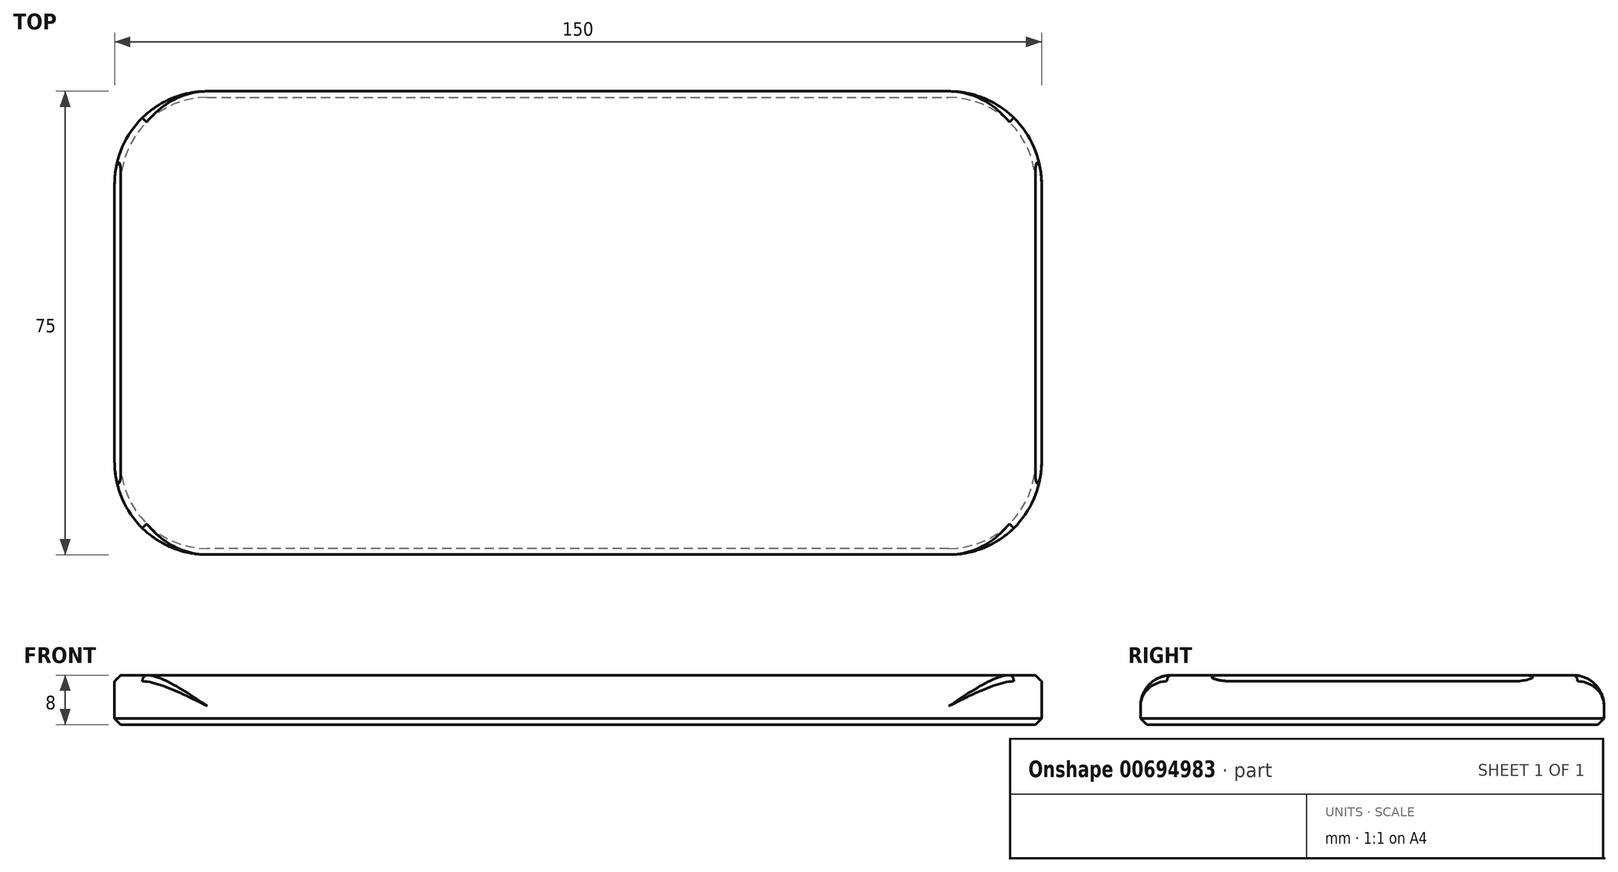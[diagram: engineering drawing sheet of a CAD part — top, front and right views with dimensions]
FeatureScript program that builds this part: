
annotation { "Feature Type Name" : "Feature", "Feature Type Description" : "" }
export const myFeature = defineFeature(function(context is Context, id is Id, definition is map)
    precondition{}
    {
        {
            var Q0;
            Q0=qCreatedBy(makeId("Top.planeOp"),FACE);
            var sketch = newSketch(context, id + "F0", { "sketchPlane" : qUnion([Q0])});
            skLineSegment(sketch, "E0.bottom", {"start": v(73.47, 26.68) * mm, "end": v(-76.53, 26.68) * mm});
            skLineSegment(sketch, "E0.top", {"start": v(73.47, -48.32) * mm, "end": v(-76.53, -48.32) * mm});
            skLineSegment(sketch, "E0.left", {"start": v(73.47, 26.68) * mm, "end": v(73.47, -48.32) * mm});
            skLineSegment(sketch, "E0.right", {"start": v(-76.53, 26.68) * mm, "end": v(-76.53, -48.32) * mm});
            skSolve(sketch);
        }
        {
            var Q0;
            Q0=makeQuery(id+"F0.imprint","IMPRINT",FACE,{"disambiguationData":[TD([[makeQuery(id+"F0.imprint","IMPRINT",EDGE,{"derivedFrom":sQuery(id+"F0.wireOp",EDGE,"E0.bottom")}),1.0]])]});
            extrude(context, id + "F1", {"entities" : qUnion([Q0]), "depth" : 8 * mm, "offsetDistance" : 25 * mm});
        }
        {
            var Q0;
            Q0=makeQuery(id+"F1.opExtrude","CAP_EDGE",EDGE,{"disambiguationData":[OSD([sQuery(id+"F0.wireOp",EDGE,"E0.left")])],"isStart":false});
            var Q1;
            Q1=makeQuery(id+"F1.opExtrude","CAP_EDGE",EDGE,{"disambiguationData":[OSD([sQuery(id+"F0.wireOp",EDGE,"E0.right")])],"isStart":false});
            chamfer(context, id + "F2", {"entities" : qUnion([Q0, Q1]), "width" : 1 * mm, "tangentPropagation" : true});
        }
        {
            var Q0;
            Q0=makeQuery(id+"F1.opExtrude","CAP_EDGE",EDGE,{"disambiguationData":[OSD([sQuery(id+"F0.wireOp",EDGE,"E0.bottom")])],"isStart":false});
            var Q1;
            Q1=makeQuery(id+"F1.opExtrude","CAP_EDGE",EDGE,{"disambiguationData":[OSD([sQuery(id+"F0.wireOp",EDGE,"E0.top")])],"isStart":false});
            fillet(context, id + "F3", {"entities" : qUnion([Q0, Q1]), "radius" : 5 * mm, "tangentPropagation" : true, "allowEdgeOverflow" : false});
        }
        {
            var Q0;
            Q0=makeQuery(id+"F1.opExtrude","SWEPT_EDGE",EDGE,{"disambiguationData":[OSD([sQuery(id+"F0.wireOp",EDGE,"E0.bottom"),sQuery(id+"F0.wireOp",EDGE,"E0.right")])]});
            var Q1;
            Q1=makeQuery(id+"F1.opExtrude","SWEPT_EDGE",EDGE,{"disambiguationData":[OSD([sQuery(id+"F0.wireOp",EDGE,"E0.top"),sQuery(id+"F0.wireOp",EDGE,"E0.left")])]});
            var Q2;
            Q2=makeQuery(id+"F1.opExtrude","SWEPT_EDGE",EDGE,{"disambiguationData":[OSD([sQuery(id+"F0.wireOp",EDGE,"E0.bottom"),sQuery(id+"F0.wireOp",EDGE,"E0.left")])]});
            var Q3;
            Q3=makeQuery(id+"F1.opExtrude","SWEPT_EDGE",EDGE,{"disambiguationData":[OSD([sQuery(id+"F0.wireOp",EDGE,"E0.top"),sQuery(id+"F0.wireOp",EDGE,"E0.right")])]});
            fillet(context, id + "F4", {"entities" : qUnion([Q0, Q1, Q2, Q3]), "radius" : 15 * mm, "tangentPropagation" : true, "allowEdgeOverflow" : false});
        }
        {
            var Q0;
            Q0=makeQuery(id+"F1.opExtrude","CAP_EDGE",EDGE,{"disambiguationData":[OSD([sQuery(id+"F0.wireOp",EDGE,"E0.left")])],"isStart":true});
            chamfer(context, id + "F5", {"entities" : qUnion([Q0]), "width" : 1 * mm, "tangentPropagation" : true});
        }
        {
            var Q0;
            {var subQ0=sQuery(id+"F0.wireOp",EDGE,"E0.left");var subQ1=sQuery(id+"F0.wireOp",EDGE,"E0.top");Q0=makeQuery(id+"F4.opFillet","BLEND_EDGE",EDGE,{"blendedFrom":[makeQuery(id+"F1.opExtrude","SWEPT_EDGE",EDGE,{"disambiguationData":[OSD([subQ1,subQ0])]}),makeQuery(id+"F1.opExtrude","CAP_FACE",FACE,{"disambiguationData":[OSD([sQuery(id+"F0.wireOp",EDGE,"E0.bottom"),subQ1,subQ0,sQuery(id+"F0.wireOp",EDGE,"E0.right")])],"isStart":false})],"blendedInto":[makeQuery(id+"F1.opExtrude","CAP_FACE",FACE,{"disambiguationData":[OSD([sQuery(id+"F0.wireOp",EDGE,"E0.bottom"),subQ1,subQ0,sQuery(id+"F0.wireOp",EDGE,"E0.right")])],"isStart":false})]});}
            var Q1;
            {var subQ0=sQuery(id+"F0.wireOp",EDGE,"E0.top");Q1=makeQuery(id+"F4.opFillet","BLEND_EDGE",EDGE,{"blendedFrom":[makeQuery(id+"F1.opExtrude","SWEPT_EDGE",EDGE,{"disambiguationData":[OSD([subQ0,sQuery(id+"F0.wireOp",EDGE,"E0.left")])]}),makeQuery(id+"F3.opFillet","BLEND_FACE",FACE,{"disambiguationData":[OSD([subQ0])]})],"blendedInto":[makeQuery(id+"F3.opFillet","BLEND_FACE",FACE,{"disambiguationData":[OSD([subQ0])]})]});}
            var Q2;
            {var subQ0=sQuery(id+"F0.wireOp",EDGE,"E0.right");var subQ1=sQuery(id+"F0.wireOp",EDGE,"E0.top");Q2=makeQuery(id+"F4.opFillet","BLEND_EDGE",EDGE,{"blendedFrom":[makeQuery(id+"F1.opExtrude","SWEPT_EDGE",EDGE,{"disambiguationData":[OSD([subQ1,subQ0])]}),makeQuery(id+"F1.opExtrude","CAP_FACE",FACE,{"disambiguationData":[OSD([sQuery(id+"F0.wireOp",EDGE,"E0.bottom"),subQ1,sQuery(id+"F0.wireOp",EDGE,"E0.left"),subQ0])],"isStart":false})],"blendedInto":[makeQuery(id+"F1.opExtrude","CAP_FACE",FACE,{"disambiguationData":[OSD([sQuery(id+"F0.wireOp",EDGE,"E0.bottom"),subQ1,sQuery(id+"F0.wireOp",EDGE,"E0.left"),subQ0])],"isStart":false})]});}
            var Q3;
            {var subQ0=sQuery(id+"F0.wireOp",EDGE,"E0.right");var subQ1=sQuery(id+"F0.wireOp",EDGE,"E0.bottom");Q3=makeQuery(id+"F4.opFillet","BLEND_EDGE",EDGE,{"blendedFrom":[makeQuery(id+"F1.opExtrude","SWEPT_EDGE",EDGE,{"disambiguationData":[OSD([subQ1,subQ0])]}),makeQuery(id+"F1.opExtrude","CAP_FACE",FACE,{"disambiguationData":[OSD([subQ1,sQuery(id+"F0.wireOp",EDGE,"E0.top"),sQuery(id+"F0.wireOp",EDGE,"E0.left"),subQ0])],"isStart":false})],"blendedInto":[makeQuery(id+"F1.opExtrude","CAP_FACE",FACE,{"disambiguationData":[OSD([subQ1,sQuery(id+"F0.wireOp",EDGE,"E0.top"),sQuery(id+"F0.wireOp",EDGE,"E0.left"),subQ0])],"isStart":false})]});}
            var Q4;
            {var subQ0=sQuery(id+"F0.wireOp",EDGE,"E0.bottom");Q4=makeQuery(id+"F4.opFillet","BLEND_EDGE",EDGE,{"blendedFrom":[makeQuery(id+"F1.opExtrude","SWEPT_EDGE",EDGE,{"disambiguationData":[OSD([subQ0,sQuery(id+"F0.wireOp",EDGE,"E0.left")])]}),makeQuery(id+"F3.opFillet","BLEND_FACE",FACE,{"disambiguationData":[OSD([subQ0])]})],"blendedInto":[makeQuery(id+"F3.opFillet","BLEND_FACE",FACE,{"disambiguationData":[OSD([subQ0])]})]});}
            var Q5;
            {var subQ0=sQuery(id+"F0.wireOp",EDGE,"E0.bottom");Q5=makeQuery(id+"F4.opFillet","BLEND_EDGE",EDGE,{"blendedFrom":[makeQuery(id+"F1.opExtrude","SWEPT_EDGE",EDGE,{"disambiguationData":[OSD([subQ0,sQuery(id+"F0.wireOp",EDGE,"E0.right")])]}),makeQuery(id+"F3.opFillet","BLEND_FACE",FACE,{"disambiguationData":[OSD([subQ0])]})],"blendedInto":[makeQuery(id+"F3.opFillet","BLEND_FACE",FACE,{"disambiguationData":[OSD([subQ0])]})]});}
            var Q6;
            {var subQ0=sQuery(id+"F0.wireOp",EDGE,"E0.left");var subQ1=sQuery(id+"F0.wireOp",EDGE,"E0.bottom");Q6=makeQuery(id+"F4.opFillet","BLEND_EDGE",EDGE,{"blendedFrom":[makeQuery(id+"F1.opExtrude","SWEPT_EDGE",EDGE,{"disambiguationData":[OSD([subQ1,subQ0])]}),makeQuery(id+"F1.opExtrude","CAP_FACE",FACE,{"disambiguationData":[OSD([subQ1,sQuery(id+"F0.wireOp",EDGE,"E0.top"),subQ0,sQuery(id+"F0.wireOp",EDGE,"E0.right")])],"isStart":false})],"blendedInto":[makeQuery(id+"F1.opExtrude","CAP_FACE",FACE,{"disambiguationData":[OSD([subQ1,sQuery(id+"F0.wireOp",EDGE,"E0.top"),subQ0,sQuery(id+"F0.wireOp",EDGE,"E0.right")])],"isStart":false})]});}
            var Q7;
            {var subQ0=sQuery(id+"F0.wireOp",EDGE,"E0.top");Q7=makeQuery(id+"F4.opFillet","BLEND_EDGE",EDGE,{"blendedFrom":[makeQuery(id+"F1.opExtrude","SWEPT_EDGE",EDGE,{"disambiguationData":[OSD([subQ0,sQuery(id+"F0.wireOp",EDGE,"E0.right")])]}),makeQuery(id+"F3.opFillet","BLEND_FACE",FACE,{"disambiguationData":[OSD([subQ0])]})],"blendedInto":[makeQuery(id+"F3.opFillet","BLEND_FACE",FACE,{"disambiguationData":[OSD([subQ0])]})]});}
            fillet(context, id + "F6", {"entities" : qUnion([Q0, Q1, Q2, Q3, Q4, Q5, Q6, Q7]), "radius" : 1 * mm, "tangentPropagation" : true, "allowEdgeOverflow" : false});
        }
    });
